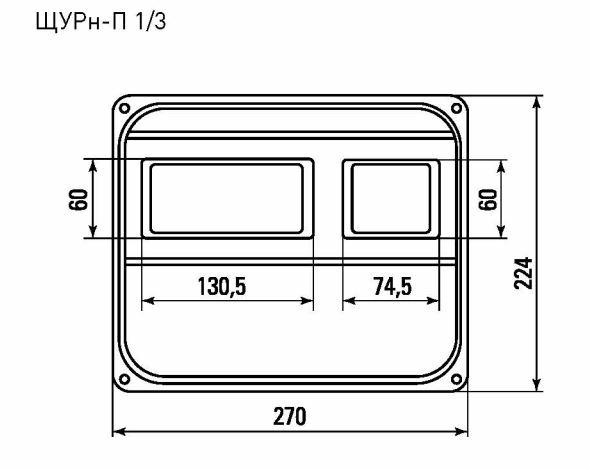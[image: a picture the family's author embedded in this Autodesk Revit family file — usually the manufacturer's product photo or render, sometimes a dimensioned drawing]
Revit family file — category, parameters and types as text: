
# Revit family: EKF_EE_Щит_Этажный_IP31_Basic
name_source: partatom
category: Электрооборудование
units: mm (PartAtom-declared; Revit-internal decimal feet)

## family parameters
Всегда вертикально = Да
На основе рабочей плоскости = Нет
Общий = Нет
При загрузке вырезать с полостями = Нет
Размер круглого соединителя = Использовать диаметр
Тип детали = Силовой щит
Точка расчета площади = Да

## types (7) — shared parameters
ADSK_Единица измерения = компл.
ADSK_Завод-изготовитель = EKF
ADSK_Количество = 1
ADSK_Материал = RAL 7035_Сталь
ADSK_Размер_Высота = 1000 мм
ADSK_Размер_Глубина = 140 мм
ADSK_Размер_Ширина = 950 мм
Изготовитель = EKF
Серия номенклатуры = PROxima
Степень защиты IP = IP31
ТВ = EKF
Тип установки = Встраиваемый
zero-valued in all types: ADSK_Масса, Количество модулей на DIN-рейке, Максимальное количество модулей

## per-type parameters (varying)
| type | ADSK_Код изделия | ADSK_Марка | ADSK_Наименование | ADSK_Обозначение | Количество DIN-реек | Описание | Тип |
| ЩЭ 7 кв. (1000х950х140) IP31 EKF Basic | mb08-v-7-bas | ЩЭ 7 кв. IP31 | Щит этажный ЩЭ 7 кв. (1000х950х140) IP31 EKF Basic | ЩЭ 7 кв. IP31 | 6 | Щит этажный ЩЭ 7 кв. (1000х950х140) IP31 EKF Basic | 189 мм |
| ЩЭ 2 кв. (1000х950х140) IP31 EKF Basic | mb08-v-2-bas | ЩЭ 2 кв. IP31 | Щит этажный ЩЭ 2 кв. (1000х950х140) IP31 EKF Basic | ЩЭ 2 кв. IP31 | 3 | Щит этажный ЩЭ 2 кв. (1000х950х140) IP31 EKF Basic | 190 мм |
| ЩЭ 3 кв. (1000х950х140) IP31 EKF Basic | mb08-v-3-bas | ЩЭ 3 кв. IP31 | Щит этажный ЩЭ 3 кв. (1000х950х140) IP31 EKF Basic | ЩЭ 3 кв. IP31 | 6 | Щит этажный ЩЭ 3 кв. (1000х950х140) IP31 EKF Basic | 191 мм |
| ЩЭ 4 кв. (1000х950х140) IP31 EKF Basic | mb08-v-4-bas | ЩЭ 4 кв. IP31 | Щит этажный ЩЭ 4 кв. (1000х950х140) IP31 EKF Basic | ЩЭ 4 кв. IP31 | 6 | Щит этажный ЩЭ 4 кв. (1000х950х140) IP31 EKF Basic | 192 мм |
| ЩЭ 4 кв. без окон (1000х950х140) IP31 EKF Basic | mb08-v-4s-bas | ЩЭ 4 кв. без окон IP31 | Щит этажный ЩЭ 4 кв. без окон (1000х950х140) IP31 EKF Basic | ЩЭ 4 кв. без окон IP31 | 6 | Щит этажный ЩЭ 4 кв. без окон (1000х950х140) IP31 EKF Basic | 193 мм |
| ЩЭ 5 кв. (1000х950х140) IP31 EKF Basic | mb08-v-5-bas | ЩЭ 5 кв. IP31 | Щит этажный ЩЭ 5 кв. (1000х950х140) IP31 EKF Basic | ЩЭ 5 кв. IP31 | 6 | Щит этажный ЩЭ 5 кв. (1000х950х140) IP31 EKF Basic | 194 мм |
| ЩЭ 6 кв. (1000х950х140) IP31 EKF Basic | mb08-v-6-bas | ЩЭ 6 кв. IP31 | Щит этажный ЩЭ 6 кв. (1000х950х140) IP31 EKF Basic | ЩЭ 6 кв. IP31 | 6 | Щит этажный ЩЭ 6 кв. (1000х950х140) IP31 EKF Basic | 195 мм |
